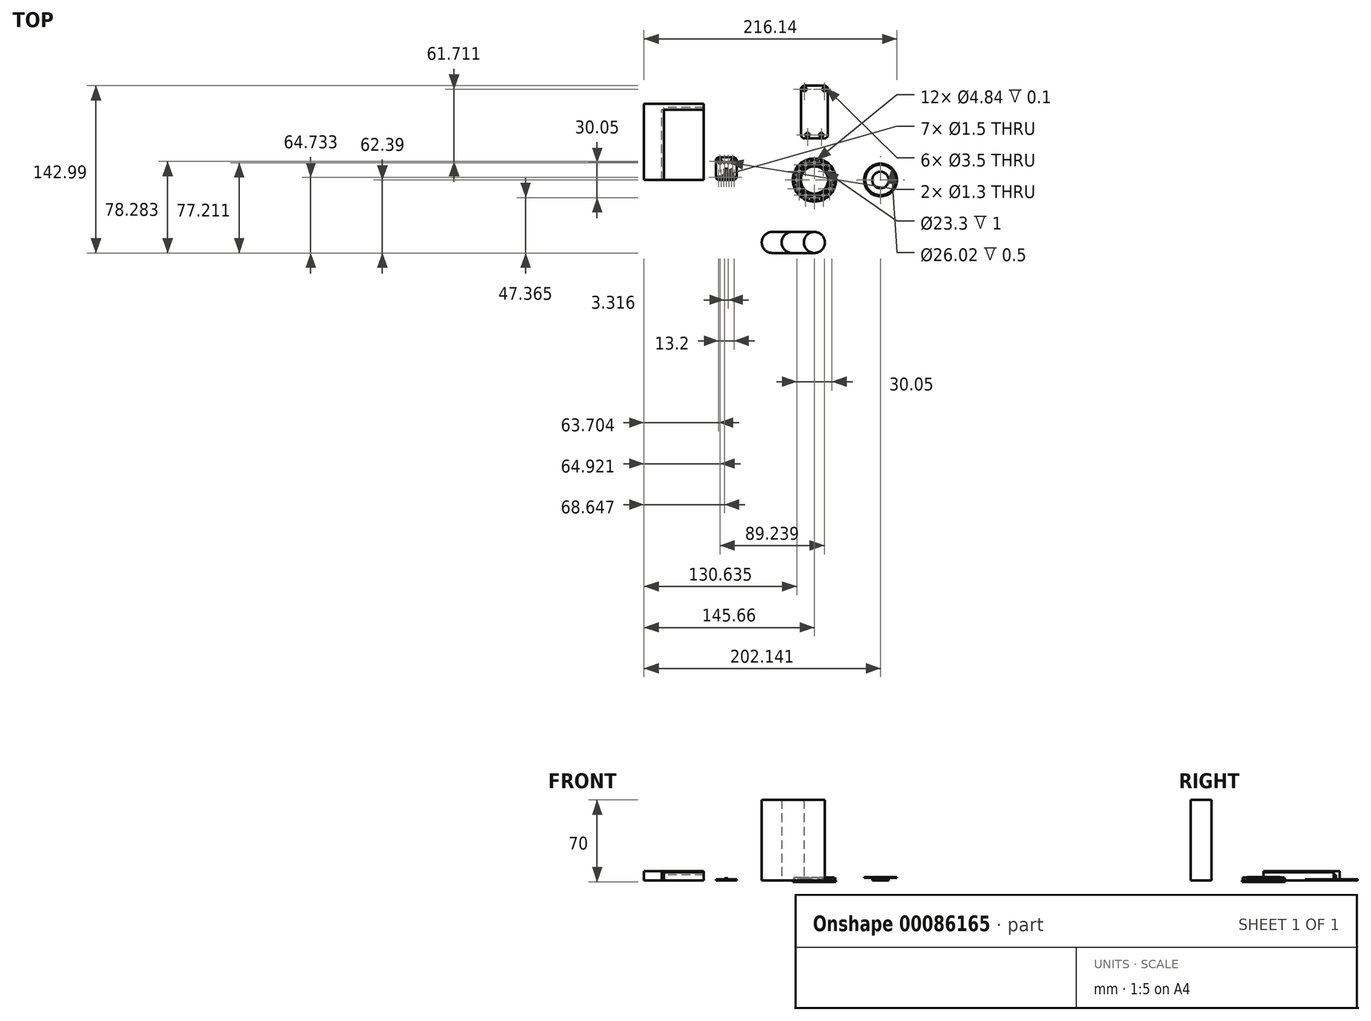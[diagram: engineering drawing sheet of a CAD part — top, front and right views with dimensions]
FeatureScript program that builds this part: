
annotation { "Feature Type Name" : "Feature", "Feature Type Description" : "" }
export const myFeature = defineFeature(function(context is Context, id is Id, definition is map)
    precondition{}
    {
        {
            var Q0;
            Q0=qCreatedBy(makeId("Top.planeOp"),FACE);
            var sketch = newSketch(context, id + "F0", { "sketchPlane" : qUnion([Q0])});
            skCircle(sketch, "E0", {"center": v(0, 0) * mm, "radius": 11.65 * mm});
            skCircle(sketch, "E1", {"center": v(0, 0) * mm, "radius": 18.4 * mm});
            skLineSegment(sketch, "E2", {"start": v(0, 18.4) * mm, "end": v(0, 11.65) * mm, "construction": true});
            skLineSegment(sketch, "E3.bottom", {"start": v(-2.95, 17.8) * mm, "end": v(2.95, 17.8) * mm});
            skLineSegment(sketch, "E3.top", {"start": v(-2.95, 12.25) * mm, "end": v(2.95, 12.25) * mm});
            skLineSegment(sketch, "E3.left", {"start": v(-2.95, 17.8) * mm, "end": v(-2.95, 12.25) * mm});
            skLineSegment(sketch, "E3.right", {"start": v(2.95, 17.8) * mm, "end": v(2.95, 12.25) * mm});
            skPoint(sketch, "E3.middle", {"position": v(0, 15.03) * mm});
            skCircle(sketch, "E4", {"center": v(0, 15.03) * mm, "radius": 2.42 * mm});
            skCircle(sketch, "E5", {"center": v(0, 0) * mm, "radius": 15.03 * mm, "construction": true});
            skPoint(sketch, "E6.1.0", {"position": v(-7.51, 13.01) * mm});
            skCircle(sketch, "E6.1.1", {"center": v(-7.51, 13.01) * mm, "radius": 2.42 * mm});
            skLineSegment(sketch, "E6.1.2", {"start": v(-6.35, 16.89) * mm, "end": v(-3.58, 12.08) * mm});
            skLineSegment(sketch, "E6.1.3", {"start": v(-11.45, 13.94) * mm, "end": v(-8.68, 9.14) * mm});
            skLineSegment(sketch, "E6.1.4", {"start": v(-8.68, 9.14) * mm, "end": v(-3.58, 12.08) * mm});
            skLineSegment(sketch, "E6.1.5", {"start": v(-11.45, 13.94) * mm, "end": v(-6.35, 16.89) * mm});
            skPoint(sketch, "E6.2.0", {"position": v(-13.01, 7.51) * mm});
            skCircle(sketch, "E6.2.1", {"center": v(-13.01, 7.51) * mm, "radius": 2.42 * mm});
            skLineSegment(sketch, "E6.2.2", {"start": v(-13.94, 11.45) * mm, "end": v(-9.14, 8.68) * mm});
            skLineSegment(sketch, "E6.2.3", {"start": v(-16.89, 6.35) * mm, "end": v(-12.08, 3.58) * mm});
            skLineSegment(sketch, "E6.2.4", {"start": v(-12.08, 3.58) * mm, "end": v(-9.14, 8.68) * mm});
            skLineSegment(sketch, "E6.2.5", {"start": v(-16.89, 6.35) * mm, "end": v(-13.94, 11.45) * mm});
            skPoint(sketch, "E6.3.0", {"position": v(-15.03, 0) * mm});
            skCircle(sketch, "E6.3.1", {"center": v(-15.03, 0) * mm, "radius": 2.42 * mm});
            skLineSegment(sketch, "E6.3.2", {"start": v(-17.8, 2.95) * mm, "end": v(-12.25, 2.95) * mm});
            skLineSegment(sketch, "E6.3.3", {"start": v(-17.8, -2.95) * mm, "end": v(-12.25, -2.95) * mm});
            skLineSegment(sketch, "E6.3.4", {"start": v(-12.25, -2.95) * mm, "end": v(-12.25, 2.95) * mm});
            skLineSegment(sketch, "E6.3.5", {"start": v(-17.8, -2.95) * mm, "end": v(-17.8, 2.95) * mm});
            skPoint(sketch, "E6.4.0", {"position": v(-13.01, -7.51) * mm});
            skCircle(sketch, "E6.4.1", {"center": v(-13.01, -7.51) * mm, "radius": 2.42 * mm});
            skLineSegment(sketch, "E6.4.2", {"start": v(-16.89, -6.35) * mm, "end": v(-12.08, -3.58) * mm});
            skLineSegment(sketch, "E6.4.3", {"start": v(-13.94, -11.45) * mm, "end": v(-9.14, -8.68) * mm});
            skLineSegment(sketch, "E6.4.4", {"start": v(-9.14, -8.68) * mm, "end": v(-12.08, -3.58) * mm});
            skLineSegment(sketch, "E6.4.5", {"start": v(-13.94, -11.45) * mm, "end": v(-16.89, -6.35) * mm});
            skPoint(sketch, "E6.5.0", {"position": v(-7.51, -13.01) * mm});
            skCircle(sketch, "E6.5.1", {"center": v(-7.51, -13.01) * mm, "radius": 2.42 * mm});
            skLineSegment(sketch, "E6.5.2", {"start": v(-11.45, -13.94) * mm, "end": v(-8.68, -9.14) * mm});
            skLineSegment(sketch, "E6.5.3", {"start": v(-6.35, -16.89) * mm, "end": v(-3.58, -12.08) * mm});
            skLineSegment(sketch, "E6.5.4", {"start": v(-3.58, -12.08) * mm, "end": v(-8.68, -9.14) * mm});
            skLineSegment(sketch, "E6.5.5", {"start": v(-6.35, -16.89) * mm, "end": v(-11.45, -13.94) * mm});
            skPoint(sketch, "E6.6.0", {"position": v(0, -15.03) * mm});
            skCircle(sketch, "E6.6.1", {"center": v(0, -15.03) * mm, "radius": 2.42 * mm});
            skLineSegment(sketch, "E6.6.2", {"start": v(-2.95, -17.8) * mm, "end": v(-2.95, -12.25) * mm});
            skLineSegment(sketch, "E6.6.3", {"start": v(2.95, -17.8) * mm, "end": v(2.95, -12.25) * mm});
            skLineSegment(sketch, "E6.6.4", {"start": v(2.95, -12.25) * mm, "end": v(-2.95, -12.25) * mm});
            skLineSegment(sketch, "E6.6.5", {"start": v(2.95, -17.8) * mm, "end": v(-2.95, -17.8) * mm});
            skPoint(sketch, "E6.7.0", {"position": v(7.51, -13.01) * mm});
            skCircle(sketch, "E6.7.1", {"center": v(7.51, -13.01) * mm, "radius": 2.42 * mm});
            skLineSegment(sketch, "E6.7.2", {"start": v(6.35, -16.89) * mm, "end": v(3.58, -12.08) * mm});
            skLineSegment(sketch, "E6.7.3", {"start": v(11.45, -13.94) * mm, "end": v(8.68, -9.14) * mm});
            skLineSegment(sketch, "E6.7.4", {"start": v(8.68, -9.14) * mm, "end": v(3.58, -12.08) * mm});
            skLineSegment(sketch, "E6.7.5", {"start": v(11.45, -13.94) * mm, "end": v(6.35, -16.89) * mm});
            skPoint(sketch, "E6.8.0", {"position": v(13.01, -7.51) * mm});
            skCircle(sketch, "E6.8.1", {"center": v(13.01, -7.51) * mm, "radius": 2.42 * mm});
            skLineSegment(sketch, "E6.8.2", {"start": v(13.94, -11.45) * mm, "end": v(9.14, -8.68) * mm});
            skLineSegment(sketch, "E6.8.3", {"start": v(16.89, -6.35) * mm, "end": v(12.08, -3.58) * mm});
            skLineSegment(sketch, "E6.8.4", {"start": v(12.08, -3.58) * mm, "end": v(9.14, -8.68) * mm});
            skLineSegment(sketch, "E6.8.5", {"start": v(16.89, -6.35) * mm, "end": v(13.94, -11.45) * mm});
            skPoint(sketch, "E6.9.0", {"position": v(15.03, 0) * mm});
            skCircle(sketch, "E6.9.1", {"center": v(15.03, 0) * mm, "radius": 2.42 * mm});
            skLineSegment(sketch, "E6.9.2", {"start": v(17.8, -2.95) * mm, "end": v(12.25, -2.95) * mm});
            skLineSegment(sketch, "E6.9.3", {"start": v(17.8, 2.95) * mm, "end": v(12.25, 2.95) * mm});
            skLineSegment(sketch, "E6.9.4", {"start": v(12.25, 2.95) * mm, "end": v(12.25, -2.95) * mm});
            skLineSegment(sketch, "E6.9.5", {"start": v(17.8, 2.95) * mm, "end": v(17.8, -2.95) * mm});
            skPoint(sketch, "E6.10.0", {"position": v(13.01, 7.51) * mm});
            skCircle(sketch, "E6.10.1", {"center": v(13.01, 7.51) * mm, "radius": 2.42 * mm});
            skLineSegment(sketch, "E6.10.2", {"start": v(16.89, 6.35) * mm, "end": v(12.08, 3.58) * mm});
            skLineSegment(sketch, "E6.10.3", {"start": v(13.94, 11.45) * mm, "end": v(9.14, 8.68) * mm});
            skLineSegment(sketch, "E6.10.4", {"start": v(9.14, 8.68) * mm, "end": v(12.08, 3.58) * mm});
            skLineSegment(sketch, "E6.10.5", {"start": v(13.94, 11.45) * mm, "end": v(16.89, 6.35) * mm});
            skPoint(sketch, "E6.11.0", {"position": v(7.51, 13.01) * mm});
            skCircle(sketch, "E6.11.1", {"center": v(7.51, 13.01) * mm, "radius": 2.42 * mm});
            skLineSegment(sketch, "E6.11.2", {"start": v(11.45, 13.94) * mm, "end": v(8.68, 9.14) * mm});
            skLineSegment(sketch, "E6.11.3", {"start": v(6.35, 16.89) * mm, "end": v(3.58, 12.08) * mm});
            skLineSegment(sketch, "E6.11.4", {"start": v(3.58, 12.08) * mm, "end": v(8.68, 9.14) * mm});
            skLineSegment(sketch, "E6.11.5", {"start": v(6.35, 16.89) * mm, "end": v(11.45, 13.94) * mm});
            skSolve(sketch);
        }
        {
            var Q0;
            Q0=makeQuery(id+"F0.imprint","IMPRINT",FACE,{"disambiguationData":[TD([[makeQuery(id+"F0.imprint","IMPRINT",EDGE,{"derivedFrom":sQuery(id+"F0.wireOp",EDGE,"E0")}),-1.0]])]});
            var Q1;
            Q1=makeQuery(id+"F0.imprint","IMPRINT",FACE,{"disambiguationData":[TD([[makeQuery(id+"F0.imprint","IMPRINT",EDGE,{"derivedFrom":sQuery(id+"F0.wireOp",EDGE,"E4")}),1.0]])]});
            var Q2;
            Q2=makeQuery(id+"F0.imprint","IMPRINT",FACE,{"disambiguationData":[TD([[makeQuery(id+"F0.imprint","IMPRINT",EDGE,{"derivedFrom":sQuery(id+"F0.wireOp",EDGE,"E6.6.1")}),-1.0]])]});
            var Q3;
            Q3=makeQuery(id+"F0.imprint","IMPRINT",FACE,{"disambiguationData":[TD([[makeQuery(id+"F0.imprint","IMPRINT",EDGE,{"derivedFrom":sQuery(id+"F0.wireOp",EDGE,"E6.7.1")}),-1.0]])]});
            var Q4;
            Q4=makeQuery(id+"F0.imprint","IMPRINT",FACE,{"disambiguationData":[TD([[makeQuery(id+"F0.imprint","IMPRINT",EDGE,{"derivedFrom":sQuery(id+"F0.wireOp",EDGE,"E6.8.1")}),-1.0]])]});
            var Q5;
            Q5=makeQuery(id+"F0.imprint","IMPRINT",FACE,{"disambiguationData":[TD([[makeQuery(id+"F0.imprint","IMPRINT",EDGE,{"derivedFrom":sQuery(id+"F0.wireOp",EDGE,"E6.9.1")}),-1.0]])]});
            var Q6;
            Q6=makeQuery(id+"F0.imprint","IMPRINT",FACE,{"disambiguationData":[TD([[makeQuery(id+"F0.imprint","IMPRINT",EDGE,{"derivedFrom":sQuery(id+"F0.wireOp",EDGE,"E6.2.1")}),-1.0]])]});
            var Q7;
            Q7=makeQuery(id+"F0.imprint","IMPRINT",FACE,{"disambiguationData":[TD([[makeQuery(id+"F0.imprint","IMPRINT",EDGE,{"derivedFrom":sQuery(id+"F0.wireOp",EDGE,"E3.bottom")}),-1.0]])]});
            var Q8;
            Q8=makeQuery(id+"F0.imprint","IMPRINT",FACE,{"disambiguationData":[TD([[makeQuery(id+"F0.imprint","IMPRINT",EDGE,{"derivedFrom":sQuery(id+"F0.wireOp",EDGE,"E6.3.1")}),-1.0]])]});
            var Q9;
            Q9=makeQuery(id+"F0.imprint","IMPRINT",FACE,{"disambiguationData":[TD([[makeQuery(id+"F0.imprint","IMPRINT",EDGE,{"derivedFrom":sQuery(id+"F0.wireOp",EDGE,"E6.1.1")}),-1.0]])]});
            var Q10;
            Q10=makeQuery(id+"F0.imprint","IMPRINT",FACE,{"disambiguationData":[TD([[makeQuery(id+"F0.imprint","IMPRINT",EDGE,{"derivedFrom":sQuery(id+"F0.wireOp",EDGE,"E6.1.1")}),1.0]])]});
            var Q11;
            Q11=makeQuery(id+"F0.imprint","IMPRINT",FACE,{"disambiguationData":[TD([[makeQuery(id+"F0.imprint","IMPRINT",EDGE,{"derivedFrom":sQuery(id+"F0.wireOp",EDGE,"E6.2.1")}),1.0]])]});
            var Q12;
            Q12=makeQuery(id+"F0.imprint","IMPRINT",FACE,{"disambiguationData":[TD([[makeQuery(id+"F0.imprint","IMPRINT",EDGE,{"derivedFrom":sQuery(id+"F0.wireOp",EDGE,"E6.3.1")}),1.0]])]});
            var Q13;
            Q13=makeQuery(id+"F0.imprint","IMPRINT",FACE,{"disambiguationData":[TD([[makeQuery(id+"F0.imprint","IMPRINT",EDGE,{"derivedFrom":sQuery(id+"F0.wireOp",EDGE,"E6.4.1")}),1.0]])]});
            var Q14;
            Q14=makeQuery(id+"F0.imprint","IMPRINT",FACE,{"disambiguationData":[TD([[makeQuery(id+"F0.imprint","IMPRINT",EDGE,{"derivedFrom":sQuery(id+"F0.wireOp",EDGE,"E6.5.1")}),1.0]])]});
            var Q15;
            Q15=makeQuery(id+"F0.imprint","IMPRINT",FACE,{"disambiguationData":[TD([[makeQuery(id+"F0.imprint","IMPRINT",EDGE,{"derivedFrom":sQuery(id+"F0.wireOp",EDGE,"E6.6.1")}),1.0]])]});
            var Q16;
            Q16=makeQuery(id+"F0.imprint","IMPRINT",FACE,{"disambiguationData":[TD([[makeQuery(id+"F0.imprint","IMPRINT",EDGE,{"derivedFrom":sQuery(id+"F0.wireOp",EDGE,"E6.7.1")}),1.0]])]});
            var Q17;
            Q17=makeQuery(id+"F0.imprint","IMPRINT",FACE,{"disambiguationData":[TD([[makeQuery(id+"F0.imprint","IMPRINT",EDGE,{"derivedFrom":sQuery(id+"F0.wireOp",EDGE,"E6.8.1")}),1.0]])]});
            var Q18;
            Q18=makeQuery(id+"F0.imprint","IMPRINT",FACE,{"disambiguationData":[TD([[makeQuery(id+"F0.imprint","IMPRINT",EDGE,{"derivedFrom":sQuery(id+"F0.wireOp",EDGE,"E6.9.1")}),1.0]])]});
            var Q19;
            Q19=makeQuery(id+"F0.imprint","IMPRINT",FACE,{"disambiguationData":[TD([[makeQuery(id+"F0.imprint","IMPRINT",EDGE,{"derivedFrom":sQuery(id+"F0.wireOp",EDGE,"E6.10.1")}),1.0]])]});
            var Q20;
            Q20=makeQuery(id+"F0.imprint","IMPRINT",FACE,{"disambiguationData":[TD([[makeQuery(id+"F0.imprint","IMPRINT",EDGE,{"derivedFrom":sQuery(id+"F0.wireOp",EDGE,"E6.11.1")}),1.0]])]});
            var Q21;
            Q21=makeQuery(id+"F0.imprint","IMPRINT",FACE,{"disambiguationData":[TD([[makeQuery(id+"F0.imprint","IMPRINT",EDGE,{"derivedFrom":sQuery(id+"F0.wireOp",EDGE,"E6.10.1")}),-1.0]])]});
            var Q22;
            Q22=makeQuery(id+"F0.imprint","IMPRINT",FACE,{"disambiguationData":[TD([[makeQuery(id+"F0.imprint","IMPRINT",EDGE,{"derivedFrom":sQuery(id+"F0.wireOp",EDGE,"E6.4.1")}),-1.0]])]});
            var Q23;
            Q23=makeQuery(id+"F0.imprint","IMPRINT",FACE,{"disambiguationData":[TD([[makeQuery(id+"F0.imprint","IMPRINT",EDGE,{"derivedFrom":sQuery(id+"F0.wireOp",EDGE,"E6.11.1")}),-1.0]])]});
            var Q24;
            Q24=makeQuery(id+"F0.imprint","IMPRINT",FACE,{"disambiguationData":[TD([[makeQuery(id+"F0.imprint","IMPRINT",EDGE,{"derivedFrom":sQuery(id+"F0.wireOp",EDGE,"E6.5.1")}),-1.0]])]});
            extrude(context, id + "F1", {"entities" : qUnion([Q0, Q1, Q2, Q3, Q4, Q5, Q6, Q7, Q8, Q9, Q10, Q11, Q12, Q13, Q14, Q15, Q16, Q17, Q18, Q19, Q20, Q21, Q22, Q23, Q24]), "oppositeDirection" : true, "depth" : 1 * mm, "offsetDistance" : 25 * mm});
        }
        {
            var Q0;
            Q0=makeQuery(id+"F0.imprint","IMPRINT",FACE,{"disambiguationData":[TD([[makeQuery(id+"F0.imprint","IMPRINT",EDGE,{"derivedFrom":sQuery(id+"F0.wireOp",EDGE,"E6.2.1")}),-1.0]])]});
            var Q1;
            Q1=makeQuery(id+"F0.imprint","IMPRINT",FACE,{"disambiguationData":[TD([[makeQuery(id+"F0.imprint","IMPRINT",EDGE,{"derivedFrom":sQuery(id+"F0.wireOp",EDGE,"E6.1.1")}),-1.0]])]});
            var Q2;
            Q2=makeQuery(id+"F0.imprint","IMPRINT",FACE,{"disambiguationData":[TD([[makeQuery(id+"F0.imprint","IMPRINT",EDGE,{"derivedFrom":sQuery(id+"F0.wireOp",EDGE,"E3.bottom")}),-1.0]])]});
            var Q3;
            Q3=makeQuery(id+"F0.imprint","IMPRINT",FACE,{"disambiguationData":[TD([[makeQuery(id+"F0.imprint","IMPRINT",EDGE,{"derivedFrom":sQuery(id+"F0.wireOp",EDGE,"E6.11.1")}),-1.0]])]});
            var Q4;
            Q4=makeQuery(id+"F0.imprint","IMPRINT",FACE,{"disambiguationData":[TD([[makeQuery(id+"F0.imprint","IMPRINT",EDGE,{"derivedFrom":sQuery(id+"F0.wireOp",EDGE,"E6.10.1")}),-1.0]])]});
            var Q5;
            Q5=makeQuery(id+"F0.imprint","IMPRINT",FACE,{"disambiguationData":[TD([[makeQuery(id+"F0.imprint","IMPRINT",EDGE,{"derivedFrom":sQuery(id+"F0.wireOp",EDGE,"E6.9.1")}),-1.0]])]});
            var Q6;
            Q6=makeQuery(id+"F0.imprint","IMPRINT",FACE,{"disambiguationData":[TD([[makeQuery(id+"F0.imprint","IMPRINT",EDGE,{"derivedFrom":sQuery(id+"F0.wireOp",EDGE,"E6.3.1")}),-1.0]])]});
            var Q7;
            Q7=makeQuery(id+"F0.imprint","IMPRINT",FACE,{"disambiguationData":[TD([[makeQuery(id+"F0.imprint","IMPRINT",EDGE,{"derivedFrom":sQuery(id+"F0.wireOp",EDGE,"E6.4.1")}),-1.0]])]});
            var Q8;
            Q8=makeQuery(id+"F0.imprint","IMPRINT",FACE,{"disambiguationData":[TD([[makeQuery(id+"F0.imprint","IMPRINT",EDGE,{"derivedFrom":sQuery(id+"F0.wireOp",EDGE,"E6.8.1")}),-1.0]])]});
            var Q9;
            Q9=makeQuery(id+"F0.imprint","IMPRINT",FACE,{"disambiguationData":[TD([[makeQuery(id+"F0.imprint","IMPRINT",EDGE,{"derivedFrom":sQuery(id+"F0.wireOp",EDGE,"E6.7.1")}),-1.0]])]});
            var Q10;
            Q10=makeQuery(id+"F0.imprint","IMPRINT",FACE,{"disambiguationData":[TD([[makeQuery(id+"F0.imprint","IMPRINT",EDGE,{"derivedFrom":sQuery(id+"F0.wireOp",EDGE,"E6.6.1")}),-1.0]])]});
            var Q11;
            Q11=makeQuery(id+"F0.imprint","IMPRINT",FACE,{"disambiguationData":[TD([[makeQuery(id+"F0.imprint","IMPRINT",EDGE,{"derivedFrom":sQuery(id+"F0.wireOp",EDGE,"E6.5.1")}),-1.0]])]});
            extrude(context, id + "F2", {"entities" : qUnion([Q0, Q1, Q2, Q3, Q4, Q5, Q6, Q7, Q8, Q9, Q10, Q11]), "operationType" : NewBodyOperationType.ADD, "depth" : 2.7 * mm, "offsetDistance" : 25 * mm});
        }
        {
            var Q0;
            Q0=makeQuery(id+"F0.imprint","IMPRINT",FACE,{"disambiguationData":[TD([[makeQuery(id+"F0.imprint","IMPRINT",EDGE,{"derivedFrom":sQuery(id+"F0.wireOp",EDGE,"E6.2.1")}),1.0]])]});
            var Q1;
            Q1=makeQuery(id+"F0.imprint","IMPRINT",FACE,{"disambiguationData":[TD([[makeQuery(id+"F0.imprint","IMPRINT",EDGE,{"derivedFrom":sQuery(id+"F0.wireOp",EDGE,"E6.1.1")}),1.0]])]});
            var Q2;
            Q2=makeQuery(id+"F0.imprint","IMPRINT",FACE,{"disambiguationData":[TD([[makeQuery(id+"F0.imprint","IMPRINT",EDGE,{"derivedFrom":sQuery(id+"F0.wireOp",EDGE,"E4")}),1.0]])]});
            var Q3;
            Q3=makeQuery(id+"F0.imprint","IMPRINT",FACE,{"disambiguationData":[TD([[makeQuery(id+"F0.imprint","IMPRINT",EDGE,{"derivedFrom":sQuery(id+"F0.wireOp",EDGE,"E6.11.1")}),1.0]])]});
            var Q4;
            Q4=makeQuery(id+"F0.imprint","IMPRINT",FACE,{"disambiguationData":[TD([[makeQuery(id+"F0.imprint","IMPRINT",EDGE,{"derivedFrom":sQuery(id+"F0.wireOp",EDGE,"E6.10.1")}),1.0]])]});
            var Q5;
            Q5=makeQuery(id+"F0.imprint","IMPRINT",FACE,{"disambiguationData":[TD([[makeQuery(id+"F0.imprint","IMPRINT",EDGE,{"derivedFrom":sQuery(id+"F0.wireOp",EDGE,"E6.9.1")}),1.0]])]});
            var Q6;
            Q6=makeQuery(id+"F0.imprint","IMPRINT",FACE,{"disambiguationData":[TD([[makeQuery(id+"F0.imprint","IMPRINT",EDGE,{"derivedFrom":sQuery(id+"F0.wireOp",EDGE,"E6.8.1")}),1.0]])]});
            var Q7;
            Q7=makeQuery(id+"F0.imprint","IMPRINT",FACE,{"disambiguationData":[TD([[makeQuery(id+"F0.imprint","IMPRINT",EDGE,{"derivedFrom":sQuery(id+"F0.wireOp",EDGE,"E6.6.1")}),1.0]])]});
            var Q8;
            Q8=makeQuery(id+"F0.imprint","IMPRINT",FACE,{"disambiguationData":[TD([[makeQuery(id+"F0.imprint","IMPRINT",EDGE,{"derivedFrom":sQuery(id+"F0.wireOp",EDGE,"E6.5.1")}),1.0]])]});
            var Q9;
            Q9=makeQuery(id+"F0.imprint","IMPRINT",FACE,{"disambiguationData":[TD([[makeQuery(id+"F0.imprint","IMPRINT",EDGE,{"derivedFrom":sQuery(id+"F0.wireOp",EDGE,"E6.4.1")}),1.0]])]});
            var Q10;
            Q10=makeQuery(id+"F0.imprint","IMPRINT",FACE,{"disambiguationData":[TD([[makeQuery(id+"F0.imprint","IMPRINT",EDGE,{"derivedFrom":sQuery(id+"F0.wireOp",EDGE,"E6.3.1")}),1.0]])]});
            var Q11;
            Q11=makeQuery(id+"F0.imprint","IMPRINT",FACE,{"disambiguationData":[TD([[makeQuery(id+"F0.imprint","IMPRINT",EDGE,{"derivedFrom":sQuery(id+"F0.wireOp",EDGE,"E6.7.1")}),1.0]])]});
            extrude(context, id + "F3", {"entities" : qUnion([Q0, Q1, Q2, Q3, Q4, Q5, Q6, Q7, Q8, Q9, Q10, Q11]), "operationType" : NewBodyOperationType.ADD, "depth" : 2.6 * mm, "offsetDistance" : 25 * mm});
        }
        {
            var Q0;
            Q0=qCreatedBy(makeId("Top.planeOp"),FACE);
            var sketch = newSketch(context, id + "F4", { "sketchPlane" : qUnion([Q0])});
            skLineSegment(sketch, "E7.bottom", {"start": v(-81.26, 0) * mm, "end": v(-69.46, 0) * mm});
            skLineSegment(sketch, "E7.top", {"start": v(-81.26, 19.4) * mm, "end": v(-69.46, 19.4) * mm});
            skLineSegment(sketch, "E7.left", {"start": v(-84.26, 3) * mm, "end": v(-84.26, 16.4) * mm});
            skLineSegment(sketch, "E7.right", {"start": v(-66.46, 3) * mm, "end": v(-66.46, 16.4) * mm});
            skLineSegment(sketch, "E8", {"start": v(-84.26, 15.9) * mm, "end": v(-66.46, 15.9) * mm, "construction": true});
            skLineSegment(sketch, "E9", {"start": v(-80.74, 19.4) * mm, "end": v(-80.74, 0) * mm, "construction": true});
            skLineSegment(sketch, "E10", {"start": v(-75.36, 19.4) * mm, "end": v(-75.36, 0) * mm, "construction": true});
            skLineSegment(sketch, "E11", {"start": v(-84.26, 2.34) * mm, "end": v(-66.46, 2.34) * mm, "construction": true});
            skLineSegment(sketch, "E12.MirrorCS", {"start": v(-69.97, 19.4) * mm, "end": v(-69.97, 0) * mm, "construction": true});
            skCircle(sketch, "E13", {"center": v(-80.74, 15.9) * mm, "radius": 1.75 * mm});
            skCircle(sketch, "E14", {"center": v(-69.97, 15.9) * mm, "radius": 1.75 * mm});
            skCircle(sketch, "E15", {"center": v(-75.36, 2.34) * mm, "radius": 0.75 * mm});
            skPoint(sketch, "E16.visualSharp", {"position": v(-84.26, 19.4) * mm});
            skArc(sketch, "E16.filletArc", {"start": v(-81.26, 19.4) * mm, "mid": v(-83.38, 18.52) * mm, "end": v(-84.26, 16.4) * mm});
            skPoint(sketch, "E17.visualSharp", {"position": v(-66.46, 19.4) * mm});
            skArc(sketch, "E17.filletArc", {"start": v(-66.46, 16.4) * mm, "mid": v(-67.33, 18.52) * mm, "end": v(-69.46, 19.4) * mm});
            skPoint(sketch, "E18.visualSharp", {"position": v(-66.46, 0) * mm});
            skArc(sketch, "E18.filletArc", {"start": v(-69.46, 0) * mm, "mid": v(-67.33, 0.88) * mm, "end": v(-66.46, 3) * mm});
            skPoint(sketch, "E19.visualSharp", {"position": v(-84.26, 0) * mm});
            skArc(sketch, "E19.filletArc", {"start": v(-84.26, 3) * mm, "mid": v(-83.38, 0.88) * mm, "end": v(-81.26, 0) * mm});
            skCircle(sketch, "E20.1.0.0", {"center": v(-73.16, 2.34) * mm, "radius": 0.75 * mm});
            skCircle(sketch, "E20.2.0.0", {"center": v(-70.96, 2.34) * mm, "radius": 0.75 * mm});
            skCircle(sketch, "E20.3.0.0", {"center": v(-68.76, 2.34) * mm, "radius": 0.75 * mm});
            skLineSegment(sketch, "E20.direction1", {"start": v(-75.36, 2.34) * mm, "end": v(-73.16, 2.34) * mm, "construction": true});
            skCircle(sketch, "E21.1.0.0", {"center": v(-77.56, 2.34) * mm, "radius": 0.75 * mm});
            skCircle(sketch, "E21.2.0.0", {"center": v(-79.76, 2.34) * mm, "radius": 0.75 * mm});
            skCircle(sketch, "E21.3.0.0", {"center": v(-81.96, 2.34) * mm, "radius": 0.75 * mm});
            skLineSegment(sketch, "E21.direction1", {"start": v(-75.36, 2.34) * mm, "end": v(-77.56, 2.34) * mm, "construction": true});
            skLineSegment(sketch, "E22.bottom", {"start": v(-76.78, 9.63) * mm, "end": v(-73.93, 9.63) * mm});
            skLineSegment(sketch, "E22.top", {"start": v(-76.78, 6.53) * mm, "end": v(-73.93, 6.53) * mm});
            skLineSegment(sketch, "E22.left", {"start": v(-76.78, 9.63) * mm, "end": v(-76.78, 6.53) * mm});
            skLineSegment(sketch, "E22.right", {"start": v(-73.93, 9.63) * mm, "end": v(-73.93, 6.53) * mm});
            skPoint(sketch, "E22.middle", {"position": v(-75.36, 8.08) * mm});
            skCircle(sketch, "E23", {"center": v(-77.01, 14.82) * mm, "radius": 0.65 * mm});
            skCircle(sketch, "E24.MirrorC", {"center": v(-73.7, 14.82) * mm, "radius": 0.65 * mm});
            skSolve(sketch);
        }
        {
            var Q0;
            Q0 = qSketchRegion(id + "F4", true);
            extrude(context, id + "F5", {"entities" : qUnion([Q0]), "depth" : 1 * mm, "offsetDistance" : 25 * mm});
        }
        {
            var Q0;
            Q0=makeQuery(id+"F4.imprint","IMPRINT",FACE,{"disambiguationData":[TD([[makeQuery(id+"F4.imprint","IMPRINT",EDGE,{"derivedFrom":sQuery(id+"F4.wireOp",EDGE,"E22.bottom")}),-1.0]])]});
            var Q1;
            Q1=sQuery(id+"F4.wireOp",EDGE,"E22.bottom");
            extrude(context, id + "F6", {"entities" : qUnion([Q0]), "operationType" : NewBodyOperationType.ADD, "surfaceEntities" : qUnion([Q1]), "depth" : 2 * mm, "offsetDistance" : 25 * mm});
        }
        {
            var Q0;
            Q0=qCreatedBy(makeId("Top.planeOp"),FACE);
            var sketch = newSketch(context, id + "F7", { "sketchPlane" : qUnion([Q0])});
            skCircle(sketch, "E25", {"center": v(56.48, 0) * mm, "radius": 14 * mm});
            skCircle(sketch, "E26", {"center": v(56.48, 0) * mm, "radius": 13.01 * mm});
            skCircle(sketch, "E27", {"center": v(56.48, 0) * mm, "radius": 5.07 * mm});
            skCircle(sketch, "E28", {"center": v(56.48, 0) * mm, "radius": 11.7 * mm});
            skCircle(sketch, "E29", {"center": v(56.48, 0) * mm, "radius": 7.09 * mm});
            skSolve(sketch);
        }
        {
            var Q0;
            Q0=makeQuery(id+"F7.imprint","IMPRINT",FACE,{"disambiguationData":[TD([[makeQuery(id+"F7.imprint","IMPRINT",EDGE,{"derivedFrom":sQuery(id+"F7.wireOp",EDGE,"E27")}),1.0]])]});
            cPlane(context, id + "F8", {"entities" : qUnion([Q0]), "cplaneType" : CPlaneType.OFFSET, "offset" : 2.5 * mm, "width" : 150 * mm, "height" : 150 * mm});
        }
        {
            var Q0;
            Q0=qCreatedBy(id+"F8.planeOp",FACE);
            var sketch = newSketch(context, id + "F9", { "sketchPlane" : qUnion([Q0])});
            skCircle(sketch, "E30.0", {"center": v(56.48, 0) * mm, "radius": 14 * mm});
            skCircle(sketch, "E31.0", {"center": v(56.48, 0) * mm, "radius": 13.01 * mm});
            skSolve(sketch);
        }
        {
            var Q0;
            Q0=makeQuery(id+"F7.imprint","IMPRINT",FACE,{"disambiguationData":[TD([[makeQuery(id+"F7.imprint","IMPRINT",EDGE,{"derivedFrom":sQuery(id+"F7.wireOp",EDGE,"E27")}),1.0]])]});
            var Q1;
            Q1=makeQuery(id+"F7.imprint","IMPRINT",FACE,{"disambiguationData":[TD([[makeQuery(id+"F7.imprint","IMPRINT",EDGE,{"derivedFrom":sQuery(id+"F7.wireOp",EDGE,"E27")}),-1.0]])]});
            extrude(context, id + "F10", {"entities" : qUnion([Q0, Q1]), "depth" : 1 * mm, "offsetDistance" : 25 * mm});
        }
        {
            var Q0;
            Q0=makeQuery(id+"F9.imprint","IMPRINT",FACE,{"disambiguationData":[TD([[makeQuery(id+"F9.imprint","IMPRINT",EDGE,{"derivedFrom":sQuery(id+"F9.wireOp",EDGE,"E30.0")}),1.0]])]});
            extrude(context, id + "F11", {"entities" : qUnion([Q0]), "depth" : 0.5 * mm});
        }
        {
            var Q0;
            Q0=makeQuery(id+"F10.opExtrude","CAP_FACE",FACE,{"disambiguationData":[OSD([sQuery(id+"F7.wireOp",EDGE,"E29")])],"isStart":false});
            var Q1;
            Q1=makeQuery(id+"F11.opExtrude","SWEPT_FACE",FACE,{"disambiguationData":[OSD([sQuery(id+"F9.wireOp",EDGE,"E31.0")])]});
            var Q2;
            Q2=makeQuery(id+"F10.opExtrude","CAP_EDGE",EDGE,{"disambiguationData":[OSD([sQuery(id+"F7.wireOp",EDGE,"E29")])],"isStart":false});
            var Q3;
            Q3=makeQuery(id+"F11.opExtrude","CAP_EDGE",EDGE,{"disambiguationData":[OSD([sQuery(id+"F9.wireOp",EDGE,"E31.0")])],"isStart":true});
            loft(context, id + "F12", {"bodyType" : ExtendedToolBodyType.SURFACE, "sheetProfilesArray" : [{ "sheetProfileEntities" : qUnion([Q0]) }, { "sheetProfileEntities" : qUnion([Q1]) }], "wireProfilesArray" : [{ "wireProfileEntities" : qUnion([Q2]) }, { "wireProfileEntities" : qUnion([Q3]) }]});
        }
        {
            var Q0;
            Q0=qCreatedBy(makeId("Top.planeOp"),FACE);
            var sketch = newSketch(context, id + "F13", { "sketchPlane" : qUnion([Q0])});
            skLineSegment(sketch, "E32.bottom", {"start": v(-8.5, 35.6) * mm, "end": v(8.5, 35.6) * mm});
            skLineSegment(sketch, "E32.top", {"start": v(-8.5, 80.6) * mm, "end": v(8.5, 80.6) * mm});
            skLineSegment(sketch, "E32.left", {"start": v(-11.5, 38.6) * mm, "end": v(-11.5, 77.6) * mm});
            skLineSegment(sketch, "E32.right", {"start": v(11.5, 38.6) * mm, "end": v(11.5, 77.6) * mm});
            skPoint(sketch, "E32.middle", {"position": v(0, 58.1) * mm});
            skPoint(sketch, "E33.visualSharp", {"position": v(-11.5, 35.6) * mm});
            skArc(sketch, "E33.filletArc", {"start": v(-11.5, 38.6) * mm, "mid": v(-10.62, 36.48) * mm, "end": v(-8.5, 35.6) * mm});
            skPoint(sketch, "E34.visualSharp", {"position": v(11.5, 35.6) * mm});
            skArc(sketch, "E34.filletArc", {"start": v(8.5, 35.6) * mm, "mid": v(10.62, 36.48) * mm, "end": v(11.5, 38.6) * mm});
            skPoint(sketch, "E35.visualSharp", {"position": v(11.5, 80.6) * mm});
            skArc(sketch, "E35.filletArc", {"start": v(11.5, 77.6) * mm, "mid": v(10.62, 79.73) * mm, "end": v(8.5, 80.6) * mm});
            skPoint(sketch, "E36.visualSharp", {"position": v(-11.5, 80.6) * mm});
            skArc(sketch, "E36.filletArc", {"start": v(-8.5, 80.6) * mm, "mid": v(-10.62, 79.73) * mm, "end": v(-11.5, 77.6) * mm});
            skLineSegment(sketch, "E37", {"start": v(0, 81.88) * mm, "end": v(0, 32.42) * mm, "construction": true});
            skLineSegment(sketch, "E38", {"start": v(19.12, 58.1) * mm, "end": v(-20.82, 58.1) * mm, "construction": true});
            skPoint(sketch, "E38.endSnap0", {"position": v(-11.5, 58.1) * mm});
            skCircle(sketch, "E39", {"center": v(-8.5, 77.6) * mm, "radius": 1.75 * mm});
            skCircle(sketch, "E40", {"center": v(8.5, 77.6) * mm, "radius": 1.75 * mm});
            skCircle(sketch, "E41", {"center": v(-5.86, 38.6) * mm, "radius": 1.75 * mm});
            skCircle(sketch, "E42.MirrorC", {"center": v(5.86, 38.6) * mm, "radius": 1.75 * mm});
            skLineSegment(sketch, "E43.bottom", {"start": v(-5.15, 80.58) * mm, "end": v(5.15, 80.58) * mm});
            skLineSegment(sketch, "E43.top", {"start": v(-5.15, 72.78) * mm, "end": v(5.15, 72.78) * mm});
            skLineSegment(sketch, "E43.left", {"start": v(-5.15, 80.58) * mm, "end": v(-5.15, 72.78) * mm});
            skLineSegment(sketch, "E43.right", {"start": v(5.15, 80.58) * mm, "end": v(5.15, 72.78) * mm});
            skPoint(sketch, "E43.middle", {"position": v(0, 76.68) * mm});
            skLineSegment(sketch, "E44.bottom", {"start": v(11.5, 70.35) * mm, "end": v(3.03, 70.35) * mm});
            skLineSegment(sketch, "E44.top", {"start": v(11.5, 62.16) * mm, "end": v(3.03, 62.16) * mm});
            skLineSegment(sketch, "E44.left", {"start": v(11.5, 70.35) * mm, "end": v(11.5, 62.16) * mm});
            skLineSegment(sketch, "E44.right", {"start": v(3.03, 70.35) * mm, "end": v(3.03, 62.16) * mm});
            skSolve(sketch);
        }
        {
            var Q0;
            Q0=makeQuery(id+"F13.imprint","IMPRINT",FACE,{"disambiguationData":[TD([[makeQuery(id+"F13.imprint","IMPRINT",EDGE,{"derivedFrom":sQuery(id+"F13.wireOp",EDGE,"E32.bottom")}),1.0]])]});
            var Q1;
            Q1=makeQuery(id+"F13.imprint","IMPRINT",FACE,{"disambiguationData":[TD([[makeQuery(id+"F13.imprint","IMPRINT",EDGE,{"derivedFrom":sQuery(id+"F13.wireOp",EDGE,"E43.bottom")}),-1.0]])]});
            var Q2;
            Q2=makeQuery(id+"F13.imprint","IMPRINT",FACE,{"disambiguationData":[TD([[makeQuery(id+"F13.imprint","IMPRINT",EDGE,{"derivedFrom":sQuery(id+"F13.wireOp",EDGE,"E44.bottom")}),1.0]])]});
            extrude(context, id + "F14", {"entities" : qUnion([Q0, Q1, Q2]), "depth" : 1 * mm, "offsetDistance" : 25 * mm});
        }
        {
            var Q0;
            Q0=qCreatedBy(makeId("Top.planeOp"),FACE);
            var sketch = newSketch(context, id + "F15", { "sketchPlane" : qUnion([Q0])});
            skCircle(sketch, "E45", {"center": v(0, -53.39) * mm, "radius": 9 * mm});
            skLineSegment(sketch, "E46", {"start": v(0, -53.39) * mm, "end": v(-60.83, -53.39) * mm, "construction": true});
            skCircle(sketch, "E47", {"center": v(-19, -53.39) * mm, "radius": 9 * mm});
            skCircle(sketch, "E48", {"center": v(-36, -53.39) * mm, "radius": 9 * mm});
            skLineSegment(sketch, "E49", {"start": v(-35.91, -44.39) * mm, "end": v(0, -44.39) * mm});
            skLineSegment(sketch, "E50", {"start": v(-36.12, -62.39) * mm, "end": v(0, -62.39) * mm});
            skSolve(sketch);
        }
        {
            var Q0;
            {var subQ0=sQuery(id+"F15.wireOp",EDGE,"E45");var subQ1=makeQuery(id+"F15.imprint","INTERSECT",VERTEX,{"derivedFrom":[subQ0,sQuery(id+"F15.wireOp",EDGE,"E49")]});Q0=makeQuery(id+"F15.imprint","IMPRINT",FACE,{"disambiguationData":[TD([[makeQuery(id+"F15.imprint","IMPRINT",EDGE,{"disambiguationData":[TD([[subQ1,-1.0]])],"derivedFrom":subQ0}),1.0]])]});}
            extrude(context, id + "F16", {"entities" : qUnion([Q0]), "depth" : 69 * mm});
        }
        {
            var Q0;
            {var subQ0=sQuery(id+"F15.wireOp",EDGE,"E47");var subQ5=sQuery(id+"F15.wireOp",EDGE,"E49");var subQ7=makeQuery(id+"F15.imprint","INTERSECT",VERTEX,{"disambiguationData":[OD(0.0)],"derivedFrom":[subQ0,subQ5]});Q0=makeQuery(id+"F15.imprint","IMPRINT",FACE,{"disambiguationData":[TD([[makeQuery(id+"F15.imprint","IMPRINT",EDGE,{"disambiguationData":[TD([[subQ7,-1.0]])],"derivedFrom":subQ0}),1.0]])]});}
            var Q1;
            {var subQ0=sQuery(id+"F15.wireOp",EDGE,"E49");var subQ1=sQuery(id+"F15.wireOp",EDGE,"E45");var subQ2=makeQuery(id+"F15.imprint","INTERSECT",VERTEX,{"derivedFrom":[subQ1,subQ0]});Q1=makeQuery(id+"F15.imprint","IMPRINT",FACE,{"disambiguationData":[TD([[makeQuery(id+"F15.imprint","IMPRINT",EDGE,{"disambiguationData":[TD([[subQ2,-1.0]])],"derivedFrom":subQ1}),-1.0]])]});}
            var Q2;
            {var subQ0=sQuery(id+"F15.wireOp",EDGE,"E48");var subQ1=sQuery(id+"F15.wireOp",EDGE,"E47");var subQ2=makeQuery(id+"F15.imprint","INTERSECT",VERTEX,{"disambiguationData":[OD(0.0)],"derivedFrom":[subQ1,subQ0]});Q2=makeQuery(id+"F15.imprint","IMPRINT",FACE,{"disambiguationData":[TD([[makeQuery(id+"F15.imprint","IMPRINT",EDGE,{"disambiguationData":[TD([[subQ2,-1.0]])],"derivedFrom":subQ1}),1.0]])]});}
            var Q3;
            {var subQ0=sQuery(id+"F15.wireOp",EDGE,"E45");var subQ1=makeQuery(id+"F15.imprint","INTERSECT",VERTEX,{"derivedFrom":[subQ0,sQuery(id+"F15.wireOp",EDGE,"E49")]});Q3=makeQuery(id+"F15.imprint","IMPRINT",FACE,{"disambiguationData":[TD([[makeQuery(id+"F15.imprint","IMPRINT",EDGE,{"disambiguationData":[TD([[subQ1,-1.0]])],"derivedFrom":subQ0}),1.0]])]});}
            extrude(context, id + "F17", {"entities" : qUnion([Q0, Q1, Q2, Q3]), "depth" : 69 * mm});
        }
        {
            var Q0;
            {var subQ0=sQuery(id+"F15.wireOp",EDGE,"E45");var subQ1=makeQuery(id+"F15.imprint","INTERSECT",VERTEX,{"derivedFrom":[subQ0,sQuery(id+"F15.wireOp",EDGE,"E49")]});Q0=makeQuery(id+"F15.imprint","IMPRINT",FACE,{"disambiguationData":[TD([[makeQuery(id+"F15.imprint","IMPRINT",EDGE,{"disambiguationData":[TD([[subQ1,-1.0]])],"derivedFrom":subQ0}),1.0]])]});}
            var Q1;
            {var subQ0=sQuery(id+"F15.wireOp",EDGE,"E49");var subQ1=sQuery(id+"F15.wireOp",EDGE,"E45");var subQ2=makeQuery(id+"F15.imprint","INTERSECT",VERTEX,{"derivedFrom":[subQ1,subQ0]});Q1=makeQuery(id+"F15.imprint","IMPRINT",FACE,{"disambiguationData":[TD([[makeQuery(id+"F15.imprint","IMPRINT",EDGE,{"disambiguationData":[TD([[subQ2,-1.0]])],"derivedFrom":subQ1}),-1.0]])]});}
            var Q2;
            {var subQ0=sQuery(id+"F15.wireOp",EDGE,"E47");var subQ5=sQuery(id+"F15.wireOp",EDGE,"E49");var subQ7=makeQuery(id+"F15.imprint","INTERSECT",VERTEX,{"disambiguationData":[OD(0.0)],"derivedFrom":[subQ0,subQ5]});Q2=makeQuery(id+"F15.imprint","IMPRINT",FACE,{"disambiguationData":[TD([[makeQuery(id+"F15.imprint","IMPRINT",EDGE,{"disambiguationData":[TD([[subQ7,-1.0]])],"derivedFrom":subQ0}),1.0]])]});}
            var Q3;
            {var subQ0=sQuery(id+"F15.wireOp",EDGE,"E49");var subQ1=sQuery(id+"F15.wireOp",EDGE,"E47");var subQ2=makeQuery(id+"F15.imprint","INTERSECT",VERTEX,{"disambiguationData":[OD(0.0)],"derivedFrom":[subQ1,subQ0]});Q3=makeQuery(id+"F15.imprint","IMPRINT",FACE,{"disambiguationData":[TD([[makeQuery(id+"F15.imprint","IMPRINT",EDGE,{"disambiguationData":[TD([[subQ2,-1.0]])],"derivedFrom":subQ1}),-1.0]])]});}
            var Q4;
            {var subQ0=sQuery(id+"F15.wireOp",EDGE,"E48");var subQ1=sQuery(id+"F15.wireOp",EDGE,"E47");var subQ2=makeQuery(id+"F15.imprint","INTERSECT",VERTEX,{"disambiguationData":[OD(0.0)],"derivedFrom":[subQ1,subQ0]});Q4=makeQuery(id+"F15.imprint","IMPRINT",FACE,{"disambiguationData":[TD([[makeQuery(id+"F15.imprint","IMPRINT",EDGE,{"disambiguationData":[TD([[subQ2,-1.0]])],"derivedFrom":subQ1}),-1.0]])]});}
            var Q5;
            {var subQ0=sQuery(id+"F15.wireOp",EDGE,"E50");var subQ1=sQuery(id+"F15.wireOp",EDGE,"E47");var subQ2=makeQuery(id+"F15.imprint","INTERSECT",VERTEX,{"derivedFrom":[subQ1,subQ0]});Q5=makeQuery(id+"F15.imprint","IMPRINT",FACE,{"disambiguationData":[TD([[makeQuery(id+"F15.imprint","IMPRINT",EDGE,{"disambiguationData":[TD([[subQ2,1.0]])],"derivedFrom":subQ1}),-1.0]])]});}
            var Q6;
            {var subQ0=sQuery(id+"F15.wireOp",EDGE,"E48");var subQ1=sQuery(id+"F15.wireOp",EDGE,"E47");var subQ2=makeQuery(id+"F15.imprint","INTERSECT",VERTEX,{"disambiguationData":[OD(0.0)],"derivedFrom":[subQ1,subQ0]});Q6=makeQuery(id+"F15.imprint","IMPRINT",FACE,{"disambiguationData":[TD([[makeQuery(id+"F15.imprint","IMPRINT",EDGE,{"disambiguationData":[TD([[subQ2,-1.0]])],"derivedFrom":subQ1}),1.0]])]});}
            extrude(context, id + "F18", {"entities" : qUnion([Q0, Q1, Q2, Q3, Q4, Q5, Q6]), "depth" : 69 * mm});
        }
        {
            var Q0;
            Q0=qCreatedBy(makeId("Top.planeOp"),FACE);
            var sketch = newSketch(context, id + "F19", { "sketchPlane" : qUnion([Q0])});
            skLineSegment(sketch, "E51.bottom", {"start": v(-94.66, 0) * mm, "end": v(-130.66, 0) * mm});
            skLineSegment(sketch, "E51.top", {"start": v(-94.66, 60) * mm, "end": v(-130.66, 60) * mm});
            skLineSegment(sketch, "E51.left", {"start": v(-94.66, 0) * mm, "end": v(-94.66, 60) * mm});
            skLineSegment(sketch, "E51.right", {"start": v(-130.66, 0) * mm, "end": v(-130.66, 60) * mm});
            skLineSegment(sketch, "E52.bottom", {"start": v(-94.66, 0) * mm, "end": v(-145.66, 0) * mm});
            skLineSegment(sketch, "E52.top", {"start": v(-94.66, 65) * mm, "end": v(-145.66, 65) * mm});
            skLineSegment(sketch, "E52.left", {"start": v(-94.66, 0) * mm, "end": v(-94.66, 65) * mm});
            skLineSegment(sketch, "E52.right", {"start": v(-145.66, 0) * mm, "end": v(-145.66, 65) * mm});
            skLineSegment(sketch, "E53.bottom", {"start": v(-94.66, 0) * mm, "end": v(-128.66, 0) * mm});
            skLineSegment(sketch, "E53.top", {"start": v(-94.66, 62) * mm, "end": v(-128.66, 62) * mm});
            skLineSegment(sketch, "E53.left", {"start": v(-94.66, 0) * mm, "end": v(-94.66, 62) * mm});
            skLineSegment(sketch, "E53.right", {"start": v(-128.66, 0) * mm, "end": v(-128.66, 62) * mm});
            skSolve(sketch);
        }
        {
            var Q0;
            {var subQ0=sQuery(id+"F19.wireOp",EDGE,"E51.top");Q0=makeQuery(id+"F19.imprint","IMPRINT",FACE,{"disambiguationData":[TD([[makeQuery(id+"F19.imprint","IMPRINT",EDGE,{"derivedFrom":subQ0}),1.0]])]});}
            extrude(context, id + "F20", {"entities" : qUnion([Q0]), "depth" : 7 * mm});
        }
        {
            var Q0;
            {var subQ0=sQuery(id+"F19.wireOp",EDGE,"E51.right");Q0=makeQuery(id+"F19.imprint","IMPRINT",FACE,{"disambiguationData":[TD([[makeQuery(id+"F19.imprint","IMPRINT",EDGE,{"derivedFrom":subQ0}),1.0]])]});}
            var Q1;
            {var subQ5=sQuery(id+"F19.wireOp",EDGE,"E53.top");Q1=makeQuery(id+"F19.imprint","IMPRINT",FACE,{"disambiguationData":[TD([[makeQuery(id+"F19.imprint","IMPRINT",EDGE,{"derivedFrom":subQ5}),1.0]])]});}
            var Q2;
            {var subQ5=sQuery(id+"F19.wireOp",EDGE,"E53.bottom");Q2=makeQuery(id+"F19.imprint","IMPRINT",FACE,{"disambiguationData":[TD([[makeQuery(id+"F19.imprint","IMPRINT",EDGE,{"derivedFrom":subQ5}),-1.0]])]});}
            var Q3;
            {var subQ0=sQuery(id+"F19.wireOp",EDGE,"E51.right");Q3=makeQuery(id+"F19.imprint","IMPRINT",FACE,{"disambiguationData":[TD([[makeQuery(id+"F19.imprint","IMPRINT",EDGE,{"derivedFrom":subQ0}),-1.0]])]});}
            extrude(context, id + "F21", {"entities" : qUnion([Q0, Q1, Q2, Q3]), "depth" : 8 * mm});
        }
        {
            var Q0;
            {var subQ5=sQuery(id+"F19.wireOp",EDGE,"E53.bottom");Q0=makeQuery(id+"F19.imprint","IMPRINT",FACE,{"disambiguationData":[TD([[makeQuery(id+"F19.imprint","IMPRINT",EDGE,{"derivedFrom":subQ5}),-1.0]])]});}
            var Q1;
            {var subQ5=sQuery(id+"F19.wireOp",EDGE,"E53.top");Q1=makeQuery(id+"F19.imprint","IMPRINT",FACE,{"disambiguationData":[TD([[makeQuery(id+"F19.imprint","IMPRINT",EDGE,{"derivedFrom":subQ5}),1.0]])]});}
            extrude(context, id + "F22", {"entities" : qUnion([Q0, Q1]), "depth" : 5 * mm});
        }
    });
